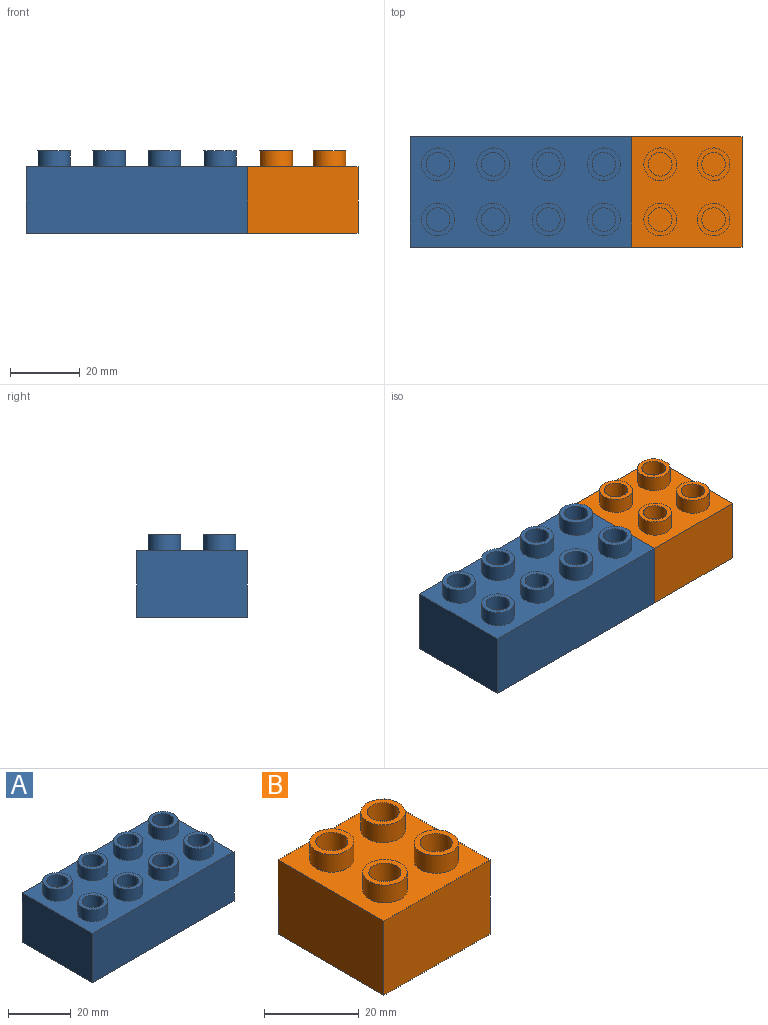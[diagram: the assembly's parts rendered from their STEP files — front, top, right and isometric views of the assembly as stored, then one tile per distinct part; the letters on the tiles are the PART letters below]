
ASSEMBLY  parts=2 mates=1
PART A: 38 faces, bbox 63.8x31.7x23.8 mm
  f0: plane 31.7x19.2mm, normal (-1,0,0), area 608.6mm2, adj f1,f3,f4,f5
  f1: plane 63.8x19.2mm, normal (0,-1,0), area 1225mm2, adj f0,f2,f4,f5
  f2: plane 31.7x19.2mm, normal (1,0,0), area 608.6mm2, adj f1,f3,f4,f5
  f3: plane 63.8x19.2mm, normal (0,1,0), area 1225mm2, adj f0,f2,f4,f5
  f4: plane 63.8x31.7mm, normal (0,0,1), area 1467.3mm2, adj f0,f1,f2,f3,f7,f11,f15,f19
  f5: plane 63.8x31.7mm, normal (0,0,-1), area 2022.5mm2, adj f0,f1,f2,f3
  f6: cylinder r=3.4mm len=6.8mm, axis (0,0,-1), area 98.3mm2, adj f8,f9
  f7: cylinder r=4.7mm len=9.4mm, axis (0,0,-1), area 135.8mm2, adj f4,f8
  f8: plane 9.4x9.4mm, normal (0,0,1), area 33.1mm2, adj f6,f7
  f9: plane 6.8x6.8mm, normal (0,0,1), area 36.3mm2, adj f6
  f10: cylinder r=3.4mm len=6.8mm, axis (0,0,-1), area 98.3mm2, adj f12,f13
  f11: cylinder r=4.7mm len=9.4mm, axis (0,0,-1), area 135.8mm2, adj f4,f12
  f12: plane 9.4x9.4mm, normal (0,0,1), area 33.1mm2, adj f10,f11
  f13: plane 6.8x6.8mm, normal (0,0,1), area 36.3mm2, adj f10
  f14: cylinder r=3.4mm len=6.8mm, axis (0,0,-1), area 98.3mm2, adj f16,f17
  f15: cylinder r=4.7mm len=9.4mm, axis (0,0,-1), area 135.8mm2, adj f4,f16
  f16: plane 9.4x9.4mm, normal (0,0,1), area 33.1mm2, adj f14,f15
  f17: plane 6.8x6.8mm, normal (0,0,1), area 36.3mm2, adj f14
  f18: cylinder r=3.4mm len=6.8mm, axis (0,0,-1), area 98.3mm2, adj f20,f21
  f19: cylinder r=4.7mm len=9.4mm, axis (0,0,-1), area 135.8mm2, adj f4,f20
  f20: plane 9.4x9.4mm, normal (0,0,1), area 33.1mm2, adj f18,f19
  f21: plane 6.8x6.8mm, normal (0,0,1), area 36.3mm2, adj f18
  f22: cylinder r=4.7mm len=9.4mm, axis (0,0,-1), area 135.8mm2, adj f4,f24
  f23: cylinder r=3.4mm len=6.8mm, axis (0,0,-1), area 98.3mm2, adj f24,f25
  f24: plane 9.4x9.4mm, normal (0,0,1), area 33.1mm2, adj f22,f23
  f25: plane 6.8x6.8mm, normal (0,0,1), area 36.3mm2, adj f23
  f26: cylinder r=4.7mm len=9.4mm, axis (0,0,-1), area 135.8mm2, adj f4,f28
  f27: cylinder r=3.4mm len=6.8mm, axis (0,0,-1), area 98.3mm2, adj f28,f29
  f28: plane 9.4x9.4mm, normal (0,0,1), area 33.1mm2, adj f26,f27
  f29: plane 6.8x6.8mm, normal (0,0,1), area 36.3mm2, adj f27
  f30: cylinder r=4.7mm len=9.4mm, axis (0,0,-1), area 135.8mm2, adj f4,f32
  f31: cylinder r=3.4mm len=6.8mm, axis (0,0,-1), area 98.3mm2, adj f32,f33
  f32: plane 9.4x9.4mm, normal (0,0,1), area 33.1mm2, adj f30,f31
  f33: plane 6.8x6.8mm, normal (0,0,1), area 36.3mm2, adj f31
  f34: cylinder r=4.7mm len=9.4mm, axis (0,0,-1), area 135.8mm2, adj f4,f36
  f35: cylinder r=3.4mm len=6.8mm, axis (0,0,-1), area 98.3mm2, adj f36,f37
  f36: plane 9.4x9.4mm, normal (0,0,1), area 33.1mm2, adj f34,f35
  f37: plane 6.8x6.8mm, normal (0,0,1), area 36.3mm2, adj f35
PART B: 22 faces, bbox 31.7x31.7x23.8 mm
  f0: plane 31.7x19.2mm, normal (-1,0,0), area 608.6mm2, adj f1,f3,f4,f5
  f1: plane 31.7x19.2mm, normal (0,-1,0), area 608.6mm2, adj f0,f2,f4,f5
  f2: plane 31.7x19.2mm, normal (1,0,0), area 608.6mm2, adj f1,f3,f4,f5
  f3: plane 31.7x19.2mm, normal (0,1,0), area 608.6mm2, adj f0,f2,f4,f5
  f4: plane 31.7x31.7mm, normal (0,0,1), area 727.3mm2, adj f0,f1,f2,f3,f7,f10,f14,f19
  f5: plane 31.7x31.7mm, normal (0,0,-1), area 1004.9mm2, adj f0,f1,f2,f3
  f6: cylinder r=3.4mm len=6.8mm, axis (0,0,-1), area 98.3mm2, adj f8,f9
  f7: cylinder r=4.7mm len=9.4mm, axis (0,0,-1), area 135.8mm2, adj f4,f8
  f8: plane 9.4x9.4mm, normal (0,0,1), area 33.1mm2, adj f6,f7
  f9: plane 6.8x6.8mm, normal (0,0,1), area 36.3mm2, adj f6
  f10: cylinder r=4.7mm len=9.4mm, axis (0,0,-1), area 135.8mm2, adj f4,f12
  f11: cylinder r=3.4mm len=6.8mm, axis (0,0,-1), area 98.3mm2, adj f12,f13
  f12: plane 9.4x9.4mm, normal (0,0,1), area 33.1mm2, adj f10,f11
  f13: plane 6.8x6.8mm, normal (0,0,1), area 36.3mm2, adj f11
  f14: cylinder r=4.7mm len=9.4mm, axis (0,0,-1), area 135.8mm2, adj f4,f16
  f15: cylinder r=3.4mm len=6.8mm, axis (0,0,-1), area 98.3mm2, adj f16,f17
  f16: plane 9.4x9.4mm, normal (0,0,1), area 33.1mm2, adj f14,f15
  f17: plane 6.8x6.8mm, normal (0,0,1), area 36.3mm2, adj f15
  f18: cylinder r=3.4mm len=6.8mm, axis (0,0,-1), area 98.3mm2, adj f20,f21
  f19: cylinder r=4.7mm len=9.4mm, axis (0,0,-1), area 135.8mm2, adj f4,f20
  f20: plane 9.4x9.4mm, normal (0,0,1), area 33.1mm2, adj f18,f19
  f21: plane 6.8x6.8mm, normal (0,0,1), area 36.3mm2, adj f18
PLACE A t=(-5.89,22.22,-14.83)mm
PLACE B t=(41.86,22.22,-14.83)mm
MATE fastened A.f2 <-> B.f0  axis (1,0,0) through (26.01,22.22,-5.23)mm
